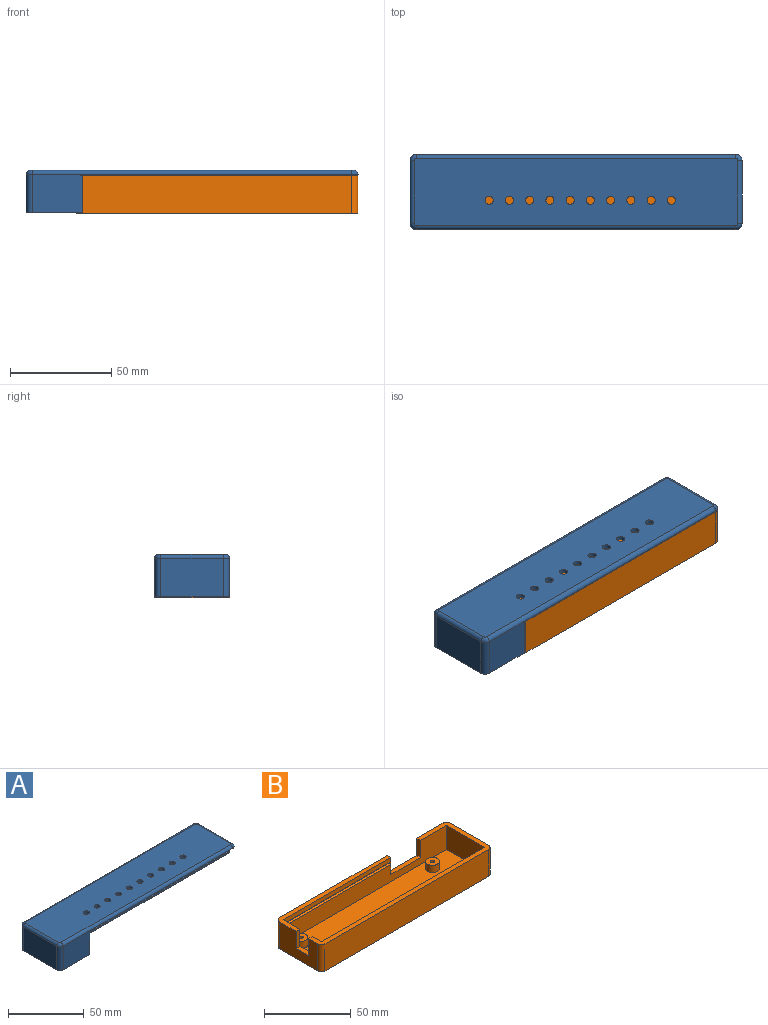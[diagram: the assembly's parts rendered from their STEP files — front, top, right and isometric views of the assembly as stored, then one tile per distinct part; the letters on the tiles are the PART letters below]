
ASSEMBLY  parts=2 mates=1
PART A: 59 faces, bbox 164x37x21 mm
  f0: plane 161x37mm, normal (0,0,-1), area 5119.5mm2, adj f4,f5,f6,f7,f8,f9,f10,f11
  f1: plane 25x19mm, normal (0,1,0), area 475mm2, adj f37,f38,f39,f57
  f2: plane 31x19mm, normal (-1,0,0), area 589mm2, adj f38,f39,f40,f53
  f3: plane 25x19mm, normal (0,-1,0), area 475mm2, adj f33,f38,f40,f52
  f4: cylinder r=2mm len=4mm, axis (0,0,-1), area 25.1mm2, adj f0,f14
  f5: cylinder r=2mm len=4mm, axis (0,0,-1), area 25.1mm2, adj f0,f14
  f6: cylinder r=2mm len=4mm, axis (0,0,-1), area 25.1mm2, adj f0,f14
  f7: cylinder r=2mm len=4mm, axis (0,0,-1), area 25.1mm2, adj f0,f14
  f8: cylinder r=2mm len=4mm, axis (0,0,-1), area 25.1mm2, adj f0,f14
  f9: cylinder r=2mm len=4mm, axis (0,0,-1), area 25.1mm2, adj f0,f14
  f10: cylinder r=2mm len=4mm, axis (0,0,-1), area 25.1mm2, adj f0,f14
  f11: cylinder r=2mm len=4mm, axis (0,0,-1), area 25.1mm2, adj f0,f14
  f12: cylinder r=2mm len=4mm, axis (0,0,-1), area 25.1mm2, adj f0,f14
  f13: cylinder r=2mm len=4mm, axis (0,0,-1), area 25.1mm2, adj f0,f14
  f14: plane 160x33mm, normal (0,0,1), area 5153.5mm2, adj f4,f5,f6,f7,f8,f9,f10,f11
  f15: plane 11.65x5mm, normal (1,0,0), area 58.3mm2, adj f0,f16,f20,f21
  f16: plane 85.49x5mm, normal (0,-1,0), area 427.4mm2, adj f0,f15,f17,f21
  f17: plane 5x2mm, normal (1,0,0), area 10mm2, adj f0,f16,f18,f21,f47
  f18: plane 87.49x3mm, normal (0,1,0), area 262.5mm2, adj f0,f17,f19,f46
  f19: plane 13.65x5mm, normal (-1,0,0), area 68.3mm2, adj f0,f18,f20,f21,f49
  f20: plane 5x2mm, normal (0,-1,0), area 10mm2, adj f0,f15,f19,f21
  f21: plane 87.49x13.65mm, normal (0,0,-1), area 198.3mm2, adj f15,f16,f17,f19,f20,f48
  f22: plane 5.35x5mm, normal (1,0,0), area 26.7mm2, adj f0,f23,f31,f32
  f23: plane 5x2mm, normal (0,1,0), area 10mm2, adj f0,f22,f24,f32
  f24: plane 7.35x5mm, normal (-1,0,0), area 36.7mm2, adj f0,f23,f25,f32,f43
  f25: plane 133x3mm, normal (0,-1,0), area 399mm2, adj f0,f24,f26,f42
  f26: plane 31x5mm, normal (1,0,0), area 155mm2, adj f0,f25,f27,f32,f41
  f27: plane 21.57x5mm, normal (0,1,0), area 107.8mm2, adj f0,f26,f28,f32
  f28: plane 5x2mm, normal (-1,0,0), area 10mm2, adj f0,f27,f29,f32
  f29: plane 19.57x5mm, normal (0,-1,0), area 97.8mm2, adj f0,f28,f30,f32
  f30: plane 27x5mm, normal (-1,0,0), area 135mm2, adj f0,f29,f31,f32
  f31: plane 129x5mm, normal (0,1,0), area 645mm2, adj f0,f22,f30,f32
  f32: plane 133x31mm, normal (0,0,-1), area 373.8mm2, adj f22,f23,f24,f26,f27,f28,f29,f30
  f33: cylinder r=3mm len=19mm, axis (0,0,1), area 89.5mm2, adj f0,f3,f34,f38
  f34: plane 22x19mm, normal (0,1,0), area 418mm2, adj f0,f33,f35,f38
  f35: plane 31x19mm, normal (1,0,0), area 589mm2, adj f0,f34,f36,f38
  f36: plane 22x19mm, normal (0,-1,0), area 418mm2, adj f0,f35,f37,f38
  f37: cylinder r=3mm len=19mm, axis (0,0,1), area 89.5mm2, adj f0,f1,f36,f38
  f38: plane 37x28mm, normal (0,0,-1), area 243mm2, adj f1,f2,f3,f33,f34,f35,f36,f37
  f39: cylinder r=3mm len=19mm, axis (0,0,1), area 89.5mm2, adj f1,f2,f38,f55
  f40: cylinder r=3mm len=19mm, axis (0,0,-1), area 89.5mm2, adj f2,f3,f38,f51
  f41: plane 2x0.5mm, normal (0.77,-0.64,0), area 1mm2, adj f26,f42,f44,f45
  f42: plane 133x0.5mm, normal (0,-0.64,0.77), area 86.5mm2, adj f25,f41,f43,f45
  f43: plane 2x0.5mm, normal (-0.77,-0.64,0), area 1mm2, adj f24,f42,f44,f45
  f44: plane 133x0.5mm, normal (0,-0.64,-0.77), area 86.5mm2, adj f32,f41,f43,f45
  f45: plane 132.16x1.16mm, normal (0,-1,0), area 153.4mm2, adj f41,f42,f43,f44
  f46: plane 87.49x0.5mm, normal (0,0.64,0.77), area 56.8mm2, adj f18,f47,f49,f50
  f47: plane 2x0.5mm, normal (0.77,0.64,0), area 1mm2, adj f17,f46,f48,f50
  f48: plane 87.49x0.5mm, normal (0,0.64,-0.77), area 56.8mm2, adj f21,f47,f49,f50
  f49: plane 2x0.5mm, normal (-0.77,0.64,0), area 1mm2, adj f19,f46,f48,f50
  f50: plane 86.65x1.16mm, normal (0,1,0), area 100.6mm2, adj f46,f47,f48,f49
  f51: torus R=1mm, axis (0,0,1), area 11.2mm2, adj f14,f40,f52,f53
  f52: cylinder r=2mm len=158mm, axis (-1,0,0), area 496.4mm2, adj f0,f3,f14,f51,f54
  f53: cylinder r=2mm len=31mm, axis (0,1,0), area 97.4mm2, adj f2,f14,f51,f55
  f54: torus R=1mm, axis (0,0,1), area 11.2mm2, adj f0,f14,f52,f56
  f55: torus R=1mm, axis (0,0,1), area 11.2mm2, adj f14,f39,f53,f57
  f56: cylinder r=2mm len=31mm, axis (0,-1,0), area 97.4mm2, adj f0,f14,f54,f58
  f57: cylinder r=2mm len=158mm, axis (1,0,0), area 496.4mm2, adj f0,f1,f14,f55,f58
  f58: torus R=1mm, axis (0,0,1), area 11.2mm2, adj f0,f14,f56,f57
PART B: 40 faces, bbox 139x37x19 mm
  f0: plane 133x12mm, normal (0,1,0), area 1596mm2, adj f3,f14,f15,f35
  f1: plane 133x3mm, normal (0,1,0), area 399mm2, adj f14,f15,f16,f37
  f2: plane 133x17mm, normal (0,-1,0), area 1535.5mm2, adj f3,f12,f14,f15,f16,f18,f21,f32
  f3: plane 133x31mm, normal (0,0,1), area 4022.5mm2, adj f0,f2,f14,f15,f22,f24
  f4: plane 133x19mm, normal (0,1,0), area 2239.6mm2, adj f10,f12,f16,f18,f19,f21,f28,f29
  f5: plane 31x19mm, normal (-1,0,0), area 469mm2, adj f10,f11,f16,f17,f19,f20,f26,f29
  f6: plane 133x19mm, normal (0,-1,0), area 2527mm2, adj f10,f16,f26,f27
  f7: cylinder r=1.25mm len=7mm, axis (0,0,1), area 55mm2, adj f10,f23
  f8: plane 31x19mm, normal (1,0,0), area 589mm2, adj f10,f16,f27,f28
  f9: cylinder r=1.25mm len=7mm, axis (0,0,1), area 55mm2, adj f10,f25
  f10: plane 139x37mm, normal (0,0,-1), area 5125.5mm2, adj f4,f5,f6,f7,f8,f9,f26,f27
  f11: plane 12x3mm, normal (0,1,0), area 36mm2, adj f5,f15,f16,f20
  f12: plane 12x3mm, normal (-1,0,0), area 36mm2, adj f2,f4,f16,f21
  f13: plane 87.62x3mm, normal (0,-1,0), area 262.9mm2, adj f15,f18,f19,f30
  f14: plane 31x17mm, normal (-1,0,0), area 527mm2, adj f0,f1,f2,f3,f16,f38
  f15: plane 31x17mm, normal (1,0,0), area 407mm2, adj f0,f1,f2,f3,f11,f13,f16,f17
  f16: plane 139x37mm, normal (0,0,1), area 599.5mm2, adj f1,f2,f4,f5,f6,f8,f11,f12
  f17: plane 12x3mm, normal (0,-1,0), area 36mm2, adj f5,f15,f19,f20
  f18: plane 12x3mm, normal (1,0,0), area 36mm2, adj f2,f4,f13,f19,f21,f33
  f19: plane 90.62x16.65mm, normal (0,0,1), area 310.9mm2, adj f4,f5,f13,f15,f17,f18,f29
  f20: plane 10x3mm, normal (0,0,1), area 30mm2, adj f5,f11,f15,f17
  f21: plane 23.95x3mm, normal (0,0,1), area 71.8mm2, adj f2,f4,f12,f18
  f22: cylinder r=4mm len=8mm, axis (0,0,-1), area 125.7mm2, adj f3,f23
  f23: plane 8x8mm, normal (0,0,1), area 45.4mm2, adj f7,f22
  f24: cylinder r=4mm len=8mm, axis (0,0,-1), area 125.7mm2, adj f3,f25
  f25: plane 8x8mm, normal (0,0,1), area 45.4mm2, adj f9,f24
  f26: cylinder r=3mm len=19mm, axis (0,0,1), area 89.5mm2, adj f5,f6,f10,f16
  f27: cylinder r=3mm len=19mm, axis (0,0,-1), area 89.5mm2, adj f6,f8,f10,f16
  f28: cylinder r=3mm len=19mm, axis (0,0,1), area 89.5mm2, adj f4,f8,f10,f16
  f29: cylinder r=3mm len=19mm, axis (0,0,-1), area 89.5mm2, adj f4,f5,f10,f19
  f30: plane 87.62x1mm, normal (0,-0.64,-0.77), area 113.3mm2, adj f13,f31,f33,f34
  f31: plane 2x1mm, normal (0.77,-0.64,0), area 1.5mm2, adj f15,f30,f32,f34
  f32: plane 87.62x1mm, normal (0,-0.64,0.77), area 113.3mm2, adj f2,f31,f33,f34
  f33: plane 2x1mm, normal (-0.77,-0.64,0), area 1.5mm2, adj f18,f30,f32,f34
  f34: plane 85.95x0.32mm, normal (0,-1,0), area 27.7mm2, adj f30,f31,f32,f33
  f35: plane 133x1mm, normal (0,0.64,0.77), area 172.5mm2, adj f0,f36,f38,f39
  f36: plane 2x1mm, normal (0.77,0.64,0), area 1.5mm2, adj f15,f35,f37,f39
  f37: plane 133x1mm, normal (0,0.64,-0.77), area 172.5mm2, adj f1,f36,f38,f39
  f38: plane 2x1mm, normal (-0.77,0.64,0), area 1.5mm2, adj f14,f35,f37,f39
  f39: plane 131.32x0.32mm, normal (0,1,0), area 42.3mm2, adj f35,f36,f37,f38
PLACE A t=(-90.3,-58.27,-13.81)mm
PLACE B t=(-37.74,-68.63,-31.18)mm fixed
MATE slider B.f16 <-> A.f0  axis (0,0,1) through (-35.41,-45.75,-14.18)mm
